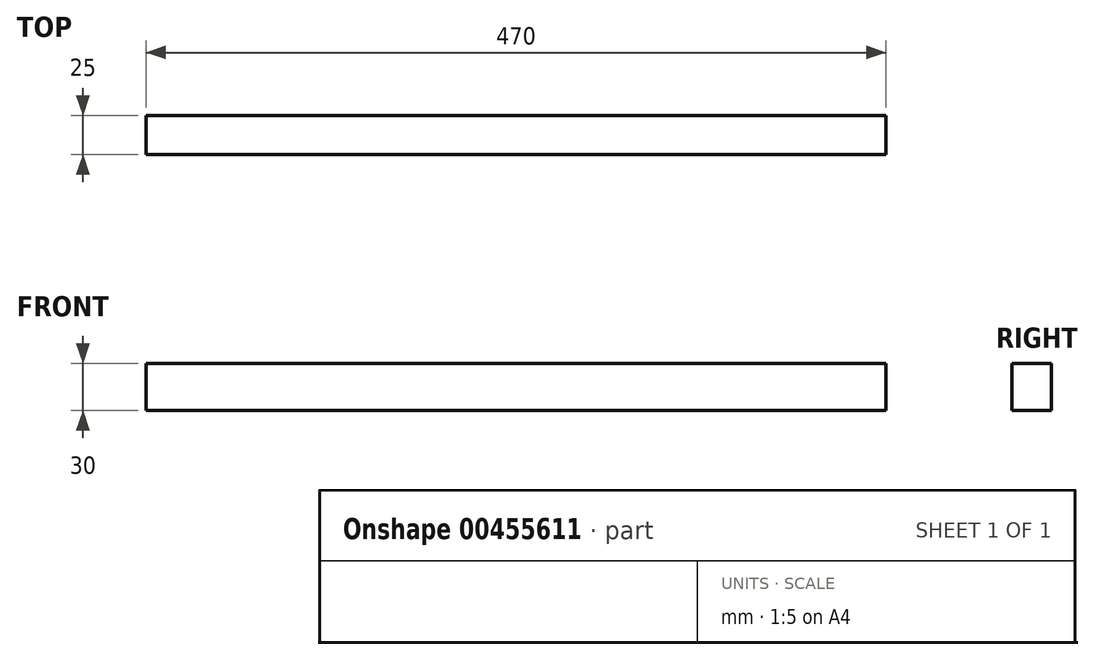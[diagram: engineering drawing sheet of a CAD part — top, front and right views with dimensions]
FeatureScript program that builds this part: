
annotation { "Feature Type Name" : "Feature", "Feature Type Description" : "" }
export const myFeature = defineFeature(function(context is Context, id is Id, definition is map)
    precondition{}
    {
        {
            var Q0;
            Q0=qCreatedBy(makeId("Front.planeOp"),FACE);
            var sketch = newSketch(context, id + "F0", { "sketchPlane" : qUnion([Q0])});
            skLineSegment(sketch, "E0.bottom", {"start": v(235, -15) * mm, "end": v(-235, -15) * mm});
            skLineSegment(sketch, "E0.top", {"start": v(235, 15) * mm, "end": v(-235, 15) * mm});
            skLineSegment(sketch, "E0.left", {"start": v(235, -15) * mm, "end": v(235, 15) * mm});
            skLineSegment(sketch, "E0.right", {"start": v(-235, -15) * mm, "end": v(-235, 15) * mm});
            skPoint(sketch, "E0.middle", {"position": v(0, 0) * mm});
            skSolve(sketch);
        }
        {
            var Q0;
            Q0 = qSketchRegion(id + "F0", true);
            extrude(context, id + "F1", {"entities" : qUnion([Q0]), "depth" : 25 * mm, "offsetDistance" : 25 * mm});
        }
    });
